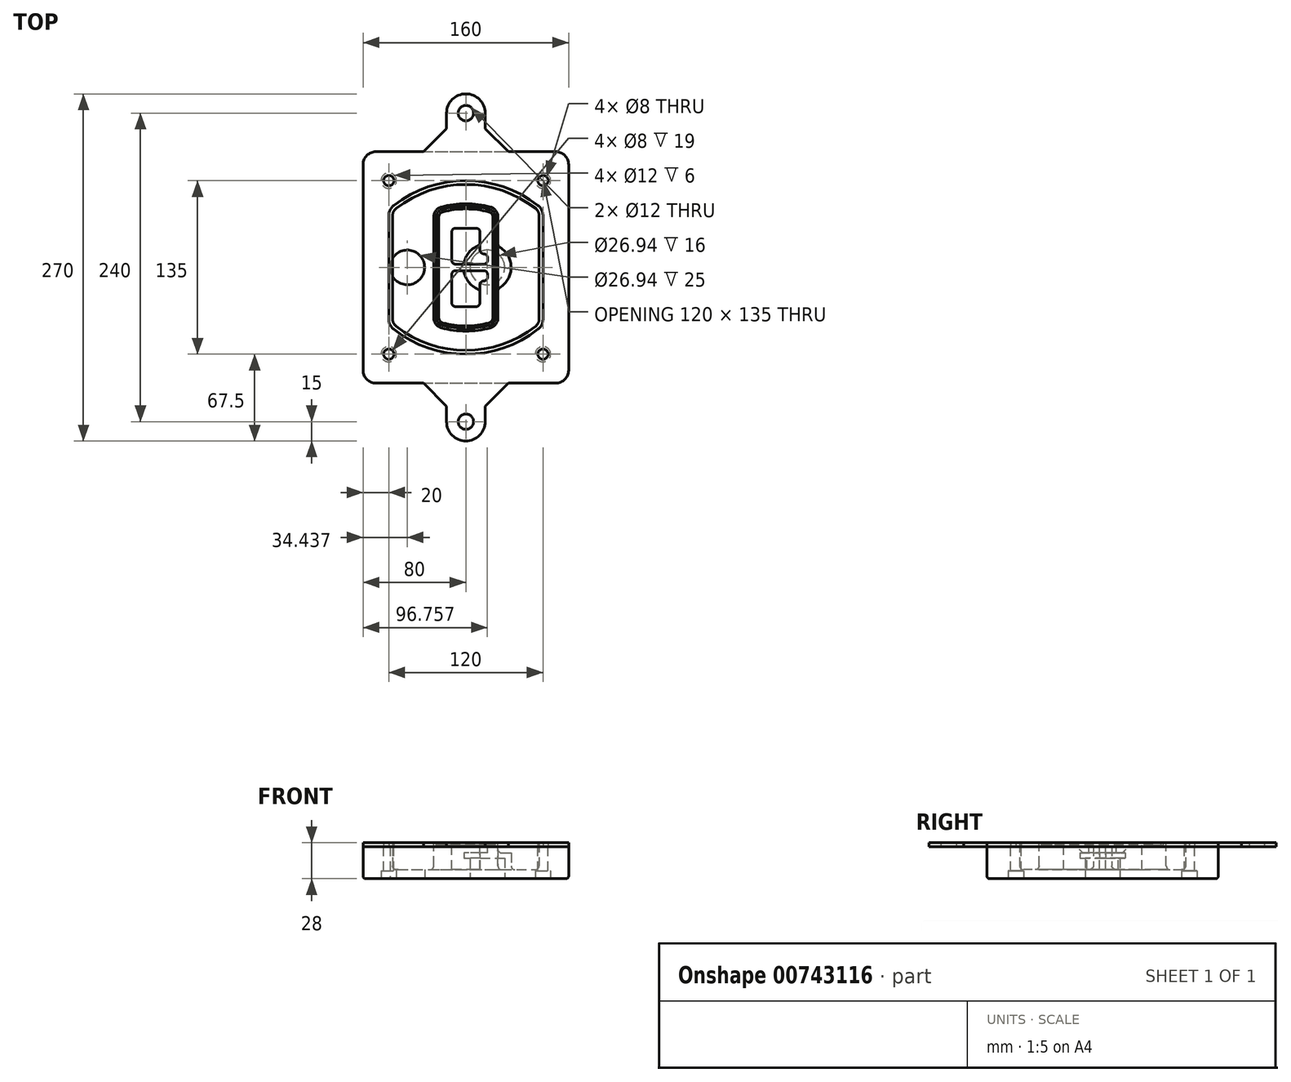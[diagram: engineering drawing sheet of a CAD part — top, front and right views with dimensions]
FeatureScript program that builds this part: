
annotation { "Feature Type Name" : "Feature", "Feature Type Description" : "" }
export const myFeature = defineFeature(function(context is Context, id is Id, definition is map)
    precondition{}
    {
        {
            var Q0;
            Q0=qCreatedBy(makeId("Top.planeOp"),FACE);
            var sketch = newSketch(context, id + "F0", { "sketchPlane" : qUnion([Q0])});
            skPoint(sketch, "E0.rect.middle", {"position": v(0, 0) * mm});
            skLineSegment(sketch, "E1.bottom", {"start": v(-70, -90) * mm, "end": v(70, -90) * mm});
            skLineSegment(sketch, "E1.top", {"start": v(-70, 90) * mm, "end": v(70, 90) * mm});
            skLineSegment(sketch, "E1.left", {"start": v(-80, -80) * mm, "end": v(-80, 80) * mm});
            skLineSegment(sketch, "E1.right", {"start": v(80, -80) * mm, "end": v(80, 80) * mm});
            skLineSegment(sketch, "E2", {"start": v(-80, 90) * mm, "end": v(80, -90) * mm, "construction": true});
            skLineSegment(sketch, "E3", {"start": v(80, 90) * mm, "end": v(-80, -90) * mm, "construction": true});
            skCircle(sketch, "E4", {"center": v(-60, 67.5) * mm, "radius": 4 * mm});
            skCircle(sketch, "E5", {"center": v(60, 67.5) * mm, "radius": 4 * mm});
            skCircle(sketch, "E6", {"center": v(60, -67.5) * mm, "radius": 4 * mm});
            skCircle(sketch, "E7", {"center": v(-60, -67.5) * mm, "radius": 4 * mm});
            skLineSegment(sketch, "E8", {"start": v(-60, 67.5) * mm, "end": v(60, 67.5) * mm, "construction": true});
            skLineSegment(sketch, "E9", {"start": v(60, 67.5) * mm, "end": v(60, -67.5) * mm, "construction": true});
            skLineSegment(sketch, "E10", {"start": v(60, -67.5) * mm, "end": v(-60, -67.5) * mm, "construction": true});
            skLineSegment(sketch, "E11", {"start": v(-60, -67.5) * mm, "end": v(-60, 67.5) * mm, "construction": true});
            skLineSegment(sketch, "E12", {"start": v(-60, 40.3) * mm, "end": v(-60, -40.3) * mm});
            skLineSegment(sketch, "E13", {"start": v(60, 40.3) * mm, "end": v(60, -40.3) * mm});
            skArc(sketch, "E14", {"start": v(56.15, 48.18) * mm, "mid": v(0, 67.5) * mm, "end": v(-56.15, 48.18) * mm});
            skArc(sketch, "E15", {"start": v(-56.15, -48.18) * mm, "mid": v(0, -67.5) * mm, "end": v(56.15, -48.18) * mm});
            skLineSegment(sketch, "E16", {"start": v(-60, 0) * mm, "end": v(60, 0) * mm, "construction": true});
            skPoint(sketch, "E17.visualSharp", {"position": v(-60, -45) * mm});
            skArc(sketch, "E17.filletArc", {"start": v(-60, -40.3) * mm, "mid": v(-58.99, -44.68) * mm, "end": v(-56.15, -48.18) * mm});
            skPoint(sketch, "E18.visualSharp", {"position": v(-60, 45) * mm});
            skArc(sketch, "E18.filletArc", {"start": v(-56.15, 48.18) * mm, "mid": v(-58.99, 44.68) * mm, "end": v(-60, 40.3) * mm});
            skPoint(sketch, "E19.visualSharp", {"position": v(60, 45) * mm});
            skArc(sketch, "E19.filletArc", {"start": v(60, 40.3) * mm, "mid": v(58.99, 44.68) * mm, "end": v(56.15, 48.18) * mm});
            skPoint(sketch, "E20.visualSharp", {"position": v(60, -45) * mm});
            skArc(sketch, "E20.filletArc", {"start": v(56.15, -48.18) * mm, "mid": v(58.99, -44.68) * mm, "end": v(60, -40.3) * mm});
            skPoint(sketch, "E21.visualSharp", {"position": v(-80, 90) * mm});
            skArc(sketch, "E21.filletArc", {"start": v(-70, 90) * mm, "mid": v(-77.07, 87.07) * mm, "end": v(-80, 80) * mm});
            skPoint(sketch, "E22.visualSharp", {"position": v(80, 90) * mm});
            skArc(sketch, "E22.filletArc", {"start": v(80, 80) * mm, "mid": v(77.07, 87.07) * mm, "end": v(70, 90) * mm});
            skPoint(sketch, "E23.visualSharp", {"position": v(80, -90) * mm});
            skArc(sketch, "E23.filletArc", {"start": v(70, -90) * mm, "mid": v(77.07, -87.07) * mm, "end": v(80, -80) * mm});
            skPoint(sketch, "E24.visualSharp", {"position": v(-80, -90) * mm});
            skArc(sketch, "E24.filletArc", {"start": v(-80, -80) * mm, "mid": v(-77.07, -87.07) * mm, "end": v(-70, -90) * mm});
            skArc(sketch, "E25.0", {"start": v(57, 40.3) * mm, "mid": v(56.3, 43.36) * mm, "end": v(54.3, 45.81) * mm});
            skLineSegment(sketch, "E25.1", {"start": v(57, 40.3) * mm, "end": v(57, -40.3) * mm});
            skArc(sketch, "E25.2", {"start": v(54.3, -45.81) * mm, "mid": v(56.3, -43.36) * mm, "end": v(57, -40.3) * mm});
            skArc(sketch, "E25.3", {"start": v(-54.3, -45.81) * mm, "mid": v(0, -64.5) * mm, "end": v(54.3, -45.81) * mm});
            skArc(sketch, "E25.4", {"start": v(-57, -40.3) * mm, "mid": v(-56.3, -43.36) * mm, "end": v(-54.3, -45.81) * mm});
            skArc(sketch, "E25.5", {"start": v(54.3, 45.81) * mm, "mid": v(0, 64.5) * mm, "end": v(-54.3, 45.81) * mm});
            skLineSegment(sketch, "E25.6", {"start": v(-57, 40.3) * mm, "end": v(-57, -40.3) * mm});
            skArc(sketch, "E25.7", {"start": v(-54.3, 45.81) * mm, "mid": v(-56.3, 43.36) * mm, "end": v(-57, 40.3) * mm});
            skArc(sketch, "E26.0", {"start": v(-58.62, 51.33) * mm, "mid": v(-62.58, 46.43) * mm, "end": v(-64, 40.3) * mm});
            skArc(sketch, "E26.1", {"start": v(58.62, 51.33) * mm, "mid": v(0, 71.5) * mm, "end": v(-58.62, 51.33) * mm});
            skArc(sketch, "E26.2", {"start": v(64, 40.3) * mm, "mid": v(62.58, 46.43) * mm, "end": v(58.62, 51.33) * mm});
            skLineSegment(sketch, "E26.3", {"start": v(64, 40.3) * mm, "end": v(64, -40.3) * mm});
            skArc(sketch, "E26.4", {"start": v(58.62, -51.33) * mm, "mid": v(62.58, -46.43) * mm, "end": v(64, -40.3) * mm});
            skLineSegment(sketch, "E26.5", {"start": v(-64, 40.3) * mm, "end": v(-64, -40.3) * mm});
            skArc(sketch, "E26.6", {"start": v(-58.62, -51.33) * mm, "mid": v(0, -71.5) * mm, "end": v(58.62, -51.33) * mm});
            skArc(sketch, "E26.7", {"start": v(-64, -40.3) * mm, "mid": v(-62.58, -46.43) * mm, "end": v(-58.62, -51.33) * mm});
            skSolve(sketch);
        }
        {
            var Q0;
            Q0=makeQuery(id+"F0.imprint","IMPRINT",FACE,{"disambiguationData":[TD([[makeQuery(id+"F0.imprint","IMPRINT",EDGE,{"derivedFrom":sQuery(id+"F0.wireOp",EDGE,"E1.bottom")}),1.0]])]});
            var Q1;
            Q1=makeQuery(id+"F0.imprint","IMPRINT",FACE,{"disambiguationData":[TD([[makeQuery(id+"F0.imprint","IMPRINT",EDGE,{"derivedFrom":sQuery(id+"F0.wireOp",EDGE,"E12")}),1.0]])]});
            var Q2;
            Q2=makeQuery(id+"F0.imprint","IMPRINT",FACE,{"disambiguationData":[TD([[makeQuery(id+"F0.imprint","IMPRINT",EDGE,{"derivedFrom":sQuery(id+"F0.wireOp",EDGE,"E25.0")}),1.0]])]});
            var Q3;
            Q3=makeQuery(id+"F0.imprint","IMPRINT",FACE,{"disambiguationData":[TD([[makeQuery(id+"F0.imprint","IMPRINT",EDGE,{"derivedFrom":sQuery(id+"F0.wireOp",EDGE,"E12")}),-1.0]])]});
            extrude(context, id + "F1", {"entities" : qUnion([Q0, Q1, Q2, Q3]), "oppositeDirection" : true, "depth" : 25 * mm});
        }
        {
            var Q0;
            Q0=makeQuery(id+"F0.imprint","IMPRINT",FACE,{"disambiguationData":[TD([[makeQuery(id+"F0.imprint","IMPRINT",EDGE,{"derivedFrom":sQuery(id+"F0.wireOp",EDGE,"E12")}),1.0]])]});
            extrude(context, id + "F2", {"entities" : qUnion([Q0]), "operationType" : NewBodyOperationType.ADD, "depth" : 3 * mm});
        }
        {
            var Q0;
            Q0=makeQuery(id+"F0.imprint","IMPRINT",FACE,{"disambiguationData":[TD([[makeQuery(id+"F0.imprint","IMPRINT",EDGE,{"derivedFrom":sQuery(id+"F0.wireOp",EDGE,"E25.0")}),1.0]])]});
            extrude(context, id + "F3", {"entities" : qUnion([Q0]), "operationType" : NewBodyOperationType.REMOVE, "oppositeDirection" : true, "depth" : 18 * mm});
        }
        {
            var Q0;
            Q0=makeQuery(id+"F2.opExtrude","CAP_FACE",FACE,{"disambiguationData":[OSD([sQuery(id+"F0.wireOp",EDGE,"E12"),sQuery(id+"F0.wireOp",EDGE,"E13"),sQuery(id+"F0.wireOp",EDGE,"E14"),sQuery(id+"F0.wireOp",EDGE,"E15"),sQuery(id+"F0.wireOp",EDGE,"E17.filletArc"),sQuery(id+"F0.wireOp",EDGE,"E18.filletArc"),sQuery(id+"F0.wireOp",EDGE,"E19.filletArc"),sQuery(id+"F0.wireOp",EDGE,"E20.filletArc"),sQuery(id+"F0.wireOp",EDGE,"E25.0"),sQuery(id+"F0.wireOp",EDGE,"E25.1"),sQuery(id+"F0.wireOp",EDGE,"E25.2"),sQuery(id+"F0.wireOp",EDGE,"E25.3"),sQuery(id+"F0.wireOp",EDGE,"E25.4"),sQuery(id+"F0.wireOp",EDGE,"E25.5"),sQuery(id+"F0.wireOp",EDGE,"E25.6"),sQuery(id+"F0.wireOp",EDGE,"E25.7")])],"isStart":false});
            var sketch = newSketch(context, id + "F4", { "sketchPlane" : qUnion([Q0])});
            skArc(sketch, "E27.0", {"start": v(-19.08, -46.97) * mm, "mid": v(0, -49.5) * mm, "end": v(19.08, -46.97) * mm});
            skArc(sketch, "E28.0", {"start": v(19.08, 46.97) * mm, "mid": v(0, 49.5) * mm, "end": v(-19.08, 46.97) * mm});
            skLineSegment(sketch, "E29", {"start": v(-25, 39.25) * mm, "end": v(-25, -39.25) * mm});
            skLineSegment(sketch, "E30", {"start": v(25, 39.25) * mm, "end": v(25, -39.25) * mm});
            skLineSegment(sketch, "E31", {"start": v(-25, 45.1) * mm, "end": v(25, 45.1) * mm, "construction": true});
            skLineSegment(sketch, "E32", {"start": v(-25, -45.1) * mm, "end": v(25, -45.1) * mm, "construction": true});
            skPoint(sketch, "E33.visualSharp", {"position": v(-25, 45.1) * mm});
            skArc(sketch, "E33.filletArc", {"start": v(-19.08, 46.97) * mm, "mid": v(-23.35, 44.11) * mm, "end": v(-25, 39.25) * mm});
            skPoint(sketch, "E34.visualSharp", {"position": v(25, 45.1) * mm});
            skArc(sketch, "E34.filletArc", {"start": v(25, 39.25) * mm, "mid": v(23.35, 44.11) * mm, "end": v(19.08, 46.97) * mm});
            skPoint(sketch, "E35.visualSharp", {"position": v(25, -45.1) * mm});
            skArc(sketch, "E35.filletArc", {"start": v(19.08, -46.97) * mm, "mid": v(23.35, -44.11) * mm, "end": v(25, -39.25) * mm});
            skPoint(sketch, "E36.visualSharp", {"position": v(-25, -45.1) * mm});
            skArc(sketch, "E36.filletArc", {"start": v(-25, -39.25) * mm, "mid": v(-23.35, -44.11) * mm, "end": v(-19.08, -46.97) * mm});
            skArc(sketch, "E37.0", {"start": v(54.3, 45.81) * mm, "mid": v(0, 64.5) * mm, "end": v(-54.3, 45.81) * mm});
            skArc(sketch, "E37.1", {"start": v(-54.3, 45.81) * mm, "mid": v(-56.3, 43.36) * mm, "end": v(-57, 40.3) * mm});
            skLineSegment(sketch, "E37.2", {"start": v(-57, 40.3) * mm, "end": v(-57, -40.3) * mm});
            skArc(sketch, "E37.3", {"start": v(-57, -40.3) * mm, "mid": v(-56.3, -43.36) * mm, "end": v(-54.3, -45.81) * mm});
            skArc(sketch, "E37.4", {"start": v(-54.3, -45.81) * mm, "mid": v(0, -64.5) * mm, "end": v(54.3, -45.81) * mm});
            skArc(sketch, "E37.5", {"start": v(54.3, -45.81) * mm, "mid": v(56.3, -43.36) * mm, "end": v(57, -40.3) * mm});
            skLineSegment(sketch, "E37.6", {"start": v(57, 40.3) * mm, "end": v(57, -40.3) * mm});
            skArc(sketch, "E37.7", {"start": v(57, 40.3) * mm, "mid": v(56.3, 43.36) * mm, "end": v(54.3, 45.81) * mm});
            skLineSegment(sketch, "E38.0", {"start": v(23, 39.25) * mm, "end": v(23, -39.25) * mm});
            skArc(sketch, "E38.1", {"start": v(18.56, -45.04) * mm, "mid": v(21.76, -42.9) * mm, "end": v(23, -39.25) * mm});
            skArc(sketch, "E38.2", {"start": v(-18.56, -45.04) * mm, "mid": v(0, -47.5) * mm, "end": v(18.56, -45.04) * mm});
            skArc(sketch, "E38.3", {"start": v(-23, -39.25) * mm, "mid": v(-21.76, -42.9) * mm, "end": v(-18.56, -45.04) * mm});
            skLineSegment(sketch, "E38.4", {"start": v(-23, 39.25) * mm, "end": v(-23, -39.25) * mm});
            skArc(sketch, "E38.5", {"start": v(23, 39.25) * mm, "mid": v(21.76, 42.9) * mm, "end": v(18.56, 45.04) * mm});
            skArc(sketch, "E38.6", {"start": v(-18.56, 45.04) * mm, "mid": v(-21.76, 42.9) * mm, "end": v(-23, 39.25) * mm});
            skArc(sketch, "E38.7", {"start": v(18.56, 45.04) * mm, "mid": v(0, 47.5) * mm, "end": v(-18.56, 45.04) * mm});
            skArc(sketch, "E39.0", {"start": v(21, 39.25) * mm, "mid": v(20.18, 41.68) * mm, "end": v(18.04, 43.1) * mm});
            skLineSegment(sketch, "E39.1", {"start": v(21, 39.25) * mm, "end": v(21, -39.25) * mm});
            skArc(sketch, "E39.2", {"start": v(18.04, -43.1) * mm, "mid": v(20.18, -41.68) * mm, "end": v(21, -39.25) * mm});
            skArc(sketch, "E39.3", {"start": v(-18.04, -43.1) * mm, "mid": v(0, -45.5) * mm, "end": v(18.04, -43.1) * mm});
            skArc(sketch, "E39.4", {"start": v(-21, -39.25) * mm, "mid": v(-20.18, -41.68) * mm, "end": v(-18.04, -43.1) * mm});
            skArc(sketch, "E39.5", {"start": v(18.04, 43.1) * mm, "mid": v(0, 45.5) * mm, "end": v(-18.04, 43.1) * mm});
            skLineSegment(sketch, "E39.6", {"start": v(-21, 39.25) * mm, "end": v(-21, -39.25) * mm});
            skArc(sketch, "E39.7", {"start": v(-18.04, 43.1) * mm, "mid": v(-20.18, 41.68) * mm, "end": v(-21, 39.25) * mm});
            skLineSegment(sketch, "E40", {"start": v(-25, 0) * mm, "end": v(25, 0) * mm, "construction": true});
            skLineSegment(sketch, "E41", {"start": v(-11, 5.5) * mm, "end": v(-11, 27.5) * mm});
            skLineSegment(sketch, "E42", {"start": v(-8, 30.5) * mm, "end": v(8, 30.5) * mm});
            skLineSegment(sketch, "E43", {"start": v(11, 27.5) * mm, "end": v(11, 13.5) * mm});
            skLineSegment(sketch, "E44", {"start": v(14, 10.5) * mm, "end": v(14, 10.5) * mm});
            skLineSegment(sketch, "E45", {"start": v(17, 7.5) * mm, "end": v(17, 5.5) * mm});
            skLineSegment(sketch, "E46", {"start": v(14, 2.5) * mm, "end": v(-8, 2.5) * mm});
            skPoint(sketch, "E47.visualSharp", {"position": v(-11, 30.5) * mm});
            skArc(sketch, "E47.filletArc", {"start": v(-8, 30.5) * mm, "mid": v(-10.12, 29.62) * mm, "end": v(-11, 27.5) * mm});
            skPoint(sketch, "E48.visualSharp", {"position": v(11, 30.5) * mm});
            skArc(sketch, "E48.filletArc", {"start": v(11, 27.5) * mm, "mid": v(10.12, 29.62) * mm, "end": v(8, 30.5) * mm});
            skPoint(sketch, "E49.visualSharp", {"position": v(11, 10.5) * mm});
            skArc(sketch, "E49.filletArc", {"start": v(11, 13.5) * mm, "mid": v(11.88, 11.38) * mm, "end": v(14, 10.5) * mm});
            skPoint(sketch, "E50.visualSharp", {"position": v(17, 10.5) * mm});
            skArc(sketch, "E50.filletArc", {"start": v(17, 7.5) * mm, "mid": v(16.12, 9.62) * mm, "end": v(14, 10.5) * mm});
            skPoint(sketch, "E51.visualSharp", {"position": v(17, 2.5) * mm});
            skArc(sketch, "E51.filletArc", {"start": v(14, 2.5) * mm, "mid": v(16.12, 3.38) * mm, "end": v(17, 5.5) * mm});
            skPoint(sketch, "E52.visualSharp", {"position": v(-11, 2.5) * mm});
            skArc(sketch, "E52.filletArc", {"start": v(-11, 5.5) * mm, "mid": v(-10.12, 3.38) * mm, "end": v(-8, 2.5) * mm});
            skLineSegment(sketch, "E53.0.MirrorCS", {"start": v(14, -2.5) * mm, "end": v(-8, -2.5) * mm});
            skArc(sketch, "E54.0.MirrorCS", {"start": v(-11, -5.5) * mm, "mid": v(-10.12, -3.38) * mm, "end": v(-8, -2.5) * mm});
            skLineSegment(sketch, "E55.0.MirrorCS", {"start": v(-11, -5.5) * mm, "end": v(-11, -27.5) * mm});
            skArc(sketch, "E56.0.MirrorCS", {"start": v(-8, -30.5) * mm, "mid": v(-10.12, -29.62) * mm, "end": v(-11, -27.5) * mm});
            skLineSegment(sketch, "E57.0.MirrorCS", {"start": v(-8, -30.5) * mm, "end": v(8, -30.5) * mm});
            skArc(sketch, "E58.0.MirrorCS", {"start": v(11, -27.5) * mm, "mid": v(10.12, -29.62) * mm, "end": v(8, -30.5) * mm});
            skLineSegment(sketch, "E59.0.MirrorCS", {"start": v(11, -27.5) * mm, "end": v(11, -13.5) * mm});
            skArc(sketch, "E60.0.MirrorCS", {"start": v(11, -13.5) * mm, "mid": v(11.88, -11.38) * mm, "end": v(14, -10.5) * mm});
            skArc(sketch, "E61.0.MirrorCS", {"start": v(17, -7.5) * mm, "mid": v(16.12, -9.62) * mm, "end": v(14, -10.5) * mm});
            skLineSegment(sketch, "E62.0.MirrorCS", {"start": v(17, -7.5) * mm, "end": v(17, -5.5) * mm});
            skArc(sketch, "E63.0.MirrorCS", {"start": v(14, -2.5) * mm, "mid": v(16.12, -3.38) * mm, "end": v(17, -5.5) * mm});
            skSolve(sketch);
        }
        {
            var Q0;
            Q0=makeQuery(id+"F4.imprint","IMPRINT",FACE,{"disambiguationData":[TD([[makeQuery(id+"F4.imprint","IMPRINT",EDGE,{"derivedFrom":sQuery(id+"F4.wireOp",EDGE,"E27.0")}),1.0]])]});
            var Q1;
            Q1=makeQuery(id+"F4.imprint","IMPRINT",FACE,{"disambiguationData":[TD([[makeQuery(id+"F4.imprint","IMPRINT",EDGE,{"derivedFrom":sQuery(id+"F4.wireOp",EDGE,"E38.0")}),-1.0]])]});
            var Q2;
            Q2=makeQuery(id+"F4.imprint","IMPRINT",FACE,{"disambiguationData":[TD([[makeQuery(id+"F4.imprint","IMPRINT",EDGE,{"derivedFrom":sQuery(id+"F4.wireOp",EDGE,"E39.0")}),1.0]])]});
            extrude(context, id + "F5", {"entities" : qUnion([Q0, Q1, Q2]), "operationType" : NewBodyOperationType.ADD, "endBound" : BoundingType.UP_TO_NEXT, "oppositeDirection" : true, "depth" : 25 * mm});
        }
        {
            var Q0;
            Q0=makeQuery(id+"F4.imprint","IMPRINT",FACE,{"disambiguationData":[TD([[makeQuery(id+"F4.imprint","IMPRINT",EDGE,{"derivedFrom":sQuery(id+"F4.wireOp",EDGE,"E38.0")}),-1.0]])]});
            extrude(context, id + "F6", {"entities" : qUnion([Q0]), "operationType" : NewBodyOperationType.REMOVE, "oppositeDirection" : true, "depth" : 2 * mm});
        }
        {
            var Q0;
            Q0=makeQuery(id+"F1.opExtrude","CAP_FACE",FACE,{"disambiguationData":[OSD([sQuery(id+"F0.wireOp",EDGE,"E1.bottom"),sQuery(id+"F0.wireOp",EDGE,"E1.top"),sQuery(id+"F0.wireOp",EDGE,"E1.left"),sQuery(id+"F0.wireOp",EDGE,"E1.right"),sQuery(id+"F0.wireOp",EDGE,"E4"),sQuery(id+"F0.wireOp",EDGE,"E5"),sQuery(id+"F0.wireOp",EDGE,"E6"),sQuery(id+"F0.wireOp",EDGE,"E7"),sQuery(id+"F0.wireOp",EDGE,"E21.filletArc"),sQuery(id+"F0.wireOp",EDGE,"E22.filletArc"),sQuery(id+"F0.wireOp",EDGE,"E23.filletArc"),sQuery(id+"F0.wireOp",EDGE,"E24.filletArc")])],"isStart":false});
            var sketch = newSketch(context, id + "F7", { "sketchPlane" : qUnion([Q0])});
            skCircle(sketch, "E64", {"center": v(16.76, 0) * mm, "radius": 13.47 * mm});
            skCircle(sketch, "E65", {"center": v(-45.56, 0) * mm, "radius": 13.47 * mm});
            skLineSegment(sketch, "E66", {"start": v(80, 0) * mm, "end": v(-80, 0) * mm});
            skCircle(sketch, "E67", {"center": v(16.76, 0) * mm, "radius": 18.47 * mm});
            skCircle(sketch, "E68", {"center": v(60, -67.5) * mm, "radius": 6 * mm});
            skCircle(sketch, "E69", {"center": v(-60, -67.5) * mm, "radius": 6 * mm});
            skCircle(sketch, "E70", {"center": v(-60, 67.5) * mm, "radius": 6 * mm});
            skCircle(sketch, "E71", {"center": v(60, 67.5) * mm, "radius": 6 * mm});
            skSolve(sketch);
        }
        {
            var Q0;
            {var subQ1=sQuery(id+"F7.wireOp",EDGE,"E66");var subQ4=sQuery(id+"F7.wireOp",EDGE,"E64");var subQ6=makeQuery(id+"F7.imprint","INTERSECT",VERTEX,{"disambiguationData":[OD(0.0)],"derivedFrom":[subQ4,subQ1]});Q0=makeQuery(id+"F7.imprint","IMPRINT",FACE,{"disambiguationData":[TD([[makeQuery(id+"F7.imprint","IMPRINT",EDGE,{"disambiguationData":[TD([[subQ6,-1.0]])],"derivedFrom":subQ4}),-1.0]])]});}
            var Q1;
            {var subQ0=sQuery(id+"F7.wireOp",EDGE,"E66");var subQ1=sQuery(id+"F7.wireOp",EDGE,"E64");var subQ3=makeQuery(id+"F7.imprint","INTERSECT",VERTEX,{"disambiguationData":[OD(0.0)],"derivedFrom":[subQ1,subQ0]});Q1=makeQuery(id+"F7.imprint","IMPRINT",FACE,{"disambiguationData":[TD([[makeQuery(id+"F7.imprint","IMPRINT",EDGE,{"disambiguationData":[TD([[subQ3,-1.0]])],"derivedFrom":subQ1}),1.0]])]});}
            var Q2;
            {var subQ0=sQuery(id+"F7.wireOp",EDGE,"E66");var subQ1=sQuery(id+"F7.wireOp",EDGE,"E64");var subQ3=makeQuery(id+"F7.imprint","INTERSECT",VERTEX,{"disambiguationData":[OD(0.0)],"derivedFrom":[subQ1,subQ0]});Q2=makeQuery(id+"F7.imprint","IMPRINT",FACE,{"disambiguationData":[TD([[makeQuery(id+"F7.imprint","IMPRINT",EDGE,{"disambiguationData":[TD([[subQ3,1.0]])],"derivedFrom":subQ1}),1.0]])]});}
            var Q3;
            {var subQ1=sQuery(id+"F7.wireOp",EDGE,"E66");var subQ4=sQuery(id+"F7.wireOp",EDGE,"E64");var subQ6=makeQuery(id+"F7.imprint","INTERSECT",VERTEX,{"disambiguationData":[OD(0.0)],"derivedFrom":[subQ4,subQ1]});Q3=makeQuery(id+"F7.imprint","IMPRINT",FACE,{"disambiguationData":[TD([[makeQuery(id+"F7.imprint","IMPRINT",EDGE,{"disambiguationData":[TD([[subQ6,1.0]])],"derivedFrom":subQ4}),-1.0]])]});}
            extrude(context, id + "F8", {"entities" : qUnion([Q0, Q1, Q2, Q3]), "operationType" : NewBodyOperationType.ADD, "oppositeDirection" : true, "depth" : 20 * mm, "offsetDistance" : 25 * mm});
        }
        {
            var Q0;
            {var subQ0=sQuery(id+"F7.wireOp",EDGE,"E66");var subQ1=sQuery(id+"F7.wireOp",EDGE,"E64");var subQ3=makeQuery(id+"F7.imprint","INTERSECT",VERTEX,{"disambiguationData":[OD(0.0)],"derivedFrom":[subQ1,subQ0]});Q0=makeQuery(id+"F7.imprint","IMPRINT",FACE,{"disambiguationData":[TD([[makeQuery(id+"F7.imprint","IMPRINT",EDGE,{"disambiguationData":[TD([[subQ3,-1.0]])],"derivedFrom":subQ1}),1.0]])]});}
            var Q1;
            {var subQ0=sQuery(id+"F7.wireOp",EDGE,"E66");var subQ1=sQuery(id+"F7.wireOp",EDGE,"E64");var subQ3=makeQuery(id+"F7.imprint","INTERSECT",VERTEX,{"disambiguationData":[OD(0.0)],"derivedFrom":[subQ1,subQ0]});Q1=makeQuery(id+"F7.imprint","IMPRINT",FACE,{"disambiguationData":[TD([[makeQuery(id+"F7.imprint","IMPRINT",EDGE,{"disambiguationData":[TD([[subQ3,1.0]])],"derivedFrom":subQ1}),1.0]])]});}
            extrude(context, id + "F9", {"entities" : qUnion([Q0, Q1]), "operationType" : NewBodyOperationType.REMOVE, "oppositeDirection" : true, "depth" : 16 * mm, "offsetDistance" : 25 * mm});
        }
        {
            var Q0;
            {var subQ0=sQuery(id+"F7.wireOp",EDGE,"E66");var subQ1=sQuery(id+"F7.wireOp",EDGE,"E65");var subQ3=makeQuery(id+"F7.imprint","INTERSECT",VERTEX,{"disambiguationData":[OD(0.0)],"derivedFrom":[subQ1,subQ0]});Q0=makeQuery(id+"F7.imprint","IMPRINT",FACE,{"disambiguationData":[TD([[makeQuery(id+"F7.imprint","IMPRINT",EDGE,{"disambiguationData":[TD([[subQ3,-1.0]])],"derivedFrom":subQ1}),1.0]])]});}
            var Q1;
            {var subQ0=sQuery(id+"F7.wireOp",EDGE,"E66");var subQ1=sQuery(id+"F7.wireOp",EDGE,"E65");var subQ3=makeQuery(id+"F7.imprint","INTERSECT",VERTEX,{"disambiguationData":[OD(0.0)],"derivedFrom":[subQ1,subQ0]});Q1=makeQuery(id+"F7.imprint","IMPRINT",FACE,{"disambiguationData":[TD([[makeQuery(id+"F7.imprint","IMPRINT",EDGE,{"disambiguationData":[TD([[subQ3,1.0]])],"derivedFrom":subQ1}),1.0]])]});}
            extrude(context, id + "F10", {"entities" : qUnion([Q0, Q1]), "operationType" : NewBodyOperationType.REMOVE, "oppositeDirection" : true, "depth" : 25 * mm, "offsetDistance" : 25 * mm});
        }
        {
            var Q0;
            Q0=makeQuery(id+"F7.imprint","IMPRINT",FACE,{"disambiguationData":[TD([[makeQuery(id+"F7.imprint","IMPRINT",EDGE,{"derivedFrom":sQuery(id+"F7.wireOp",EDGE,"E68")}),1.0]])]});
            var Q1;
            Q1=makeQuery(id+"F7.imprint","IMPRINT",FACE,{"disambiguationData":[TD([[makeQuery(id+"F7.imprint","IMPRINT",EDGE,{"derivedFrom":makeQuery(id+"F1.opExtrude","CAP_EDGE",EDGE,{"disambiguationData":[OSD([sQuery(id+"F0.wireOp",EDGE,"E5")])],"isStart":false})}),-1.0]])]});
            var Q2;
            Q2=makeQuery(id+"F7.imprint","IMPRINT",FACE,{"disambiguationData":[TD([[makeQuery(id+"F7.imprint","IMPRINT",EDGE,{"derivedFrom":sQuery(id+"F7.wireOp",EDGE,"E69")}),1.0]])]});
            var Q3;
            Q3=makeQuery(id+"F7.imprint","IMPRINT",FACE,{"disambiguationData":[TD([[makeQuery(id+"F7.imprint","IMPRINT",EDGE,{"derivedFrom":makeQuery(id+"F1.opExtrude","CAP_EDGE",EDGE,{"disambiguationData":[OSD([sQuery(id+"F0.wireOp",EDGE,"E4")])],"isStart":false})}),-1.0]])]});
            var Q4;
            Q4=makeQuery(id+"F7.imprint","IMPRINT",FACE,{"disambiguationData":[TD([[makeQuery(id+"F7.imprint","IMPRINT",EDGE,{"derivedFrom":sQuery(id+"F7.wireOp",EDGE,"E70")}),1.0]])]});
            var Q5;
            Q5=makeQuery(id+"F7.imprint","IMPRINT",FACE,{"disambiguationData":[TD([[makeQuery(id+"F7.imprint","IMPRINT",EDGE,{"derivedFrom":makeQuery(id+"F1.opExtrude","CAP_EDGE",EDGE,{"disambiguationData":[OSD([sQuery(id+"F0.wireOp",EDGE,"E7")])],"isStart":false})}),-1.0]])]});
            var Q6;
            Q6=makeQuery(id+"F7.imprint","IMPRINT",FACE,{"disambiguationData":[TD([[makeQuery(id+"F7.imprint","IMPRINT",EDGE,{"derivedFrom":sQuery(id+"F7.wireOp",EDGE,"E71")}),1.0]])]});
            var Q7;
            Q7=makeQuery(id+"F7.imprint","IMPRINT",FACE,{"disambiguationData":[TD([[makeQuery(id+"F7.imprint","IMPRINT",EDGE,{"derivedFrom":makeQuery(id+"F1.opExtrude","CAP_EDGE",EDGE,{"disambiguationData":[OSD([sQuery(id+"F0.wireOp",EDGE,"E6")])],"isStart":false})}),-1.0]])]});
            extrude(context, id + "F11", {"entities" : qUnion([Q0, Q1, Q2, Q3, Q4, Q5, Q6, Q7]), "operationType" : NewBodyOperationType.REMOVE, "oppositeDirection" : true, "depth" : 6 * mm});
        }
        {
            var Q0;
            Q0=makeQuery(id+"F9.boolean.opBoolean","COPY",FACE,{"derivedFrom":makeQuery(id+"F9.opExtrude","CAP_FACE",FACE,{"disambiguationData":[OSD([sQuery(id+"F7.wireOp",EDGE,"E64")])],"isStart":false})});
            var sketch = newSketch(context, id + "F12", { "sketchPlane" : qUnion([Q0])});
            skArc(sketch, "E72.0", {"start": v(11, 17.55) * mm, "mid": v(2.57, 11.82) * mm, "end": v(-1.54, 2.5) * mm});
            skArc(sketch, "E72.1", {"start": v(-1.54, -2.5) * mm, "mid": v(2.57, -11.82) * mm, "end": v(11, -17.55) * mm});
            skLineSegment(sketch, "E73", {"start": v(-1.54, -2.5) * mm, "end": v(14, -2.5) * mm});
            skLineSegment(sketch, "E74.0", {"start": v(14, 2.5) * mm, "end": v(-1.54, 2.5) * mm});
            skArc(sketch, "E74.1", {"start": v(14, 2.5) * mm, "mid": v(16.12, 3.38) * mm, "end": v(17, 5.5) * mm});
            skLineSegment(sketch, "E74.2", {"start": v(17, 7.5) * mm, "end": v(17, 5.5) * mm});
            skArc(sketch, "E74.3", {"start": v(17, 7.5) * mm, "mid": v(16.12, 9.62) * mm, "end": v(14, 10.5) * mm});
            skArc(sketch, "E74.4", {"start": v(11, 13.5) * mm, "mid": v(11.88, 11.38) * mm, "end": v(14, 10.5) * mm});
            skLineSegment(sketch, "E74.5", {"start": v(11, 17.55) * mm, "end": v(11, 13.5) * mm});
            skLineSegment(sketch, "E74.7", {"start": v(14, -2.5) * mm, "end": v(-1.54, -2.5) * mm});
            skArc(sketch, "E74.8", {"start": v(14, -2.5) * mm, "mid": v(16.12, -3.38) * mm, "end": v(17, -5.5) * mm});
            skLineSegment(sketch, "E74.9", {"start": v(17, -7.5) * mm, "end": v(17, -5.5) * mm});
            skArc(sketch, "E74.10", {"start": v(17, -7.5) * mm, "mid": v(16.12, -9.62) * mm, "end": v(14, -10.5) * mm});
            skArc(sketch, "E74.11", {"start": v(11, -13.5) * mm, "mid": v(11.88, -11.38) * mm, "end": v(14, -10.5) * mm});
            skLineSegment(sketch, "E74.12", {"start": v(11, -17.55) * mm, "end": v(11, -13.5) * mm});
            skPoint(sketch, "E75.orphan", {"position": v(11, -27.5) * mm});
            skPoint(sketch, "E76.orphan", {"position": v(-8, -2.5) * mm});
            skPoint(sketch, "E77.orphan", {"position": v(-8, 2.5) * mm});
            skPoint(sketch, "E78.orphan", {"position": v(11, 27.5) * mm});
            skSolve(sketch);
        }
        {
            var Q0;
            {var subQ7=sQuery(id+"F12.wireOp",EDGE,"E72.0");var subQ14=sQuery(id+"F12.wireOp",EDGE,"E72.1");var subQ16=sQuery(id+"F12.wireOp",EDGE,"E74.1");var subQ18=sQuery(id+"F12.wireOp",EDGE,"E74.8");Q0=qUnion([makeQuery(id+"F12.imprint","IMPRINT",FACE,{"disambiguationData":[TD([[makeQuery(id+"F12.imprint","IMPRINT",EDGE,{"derivedFrom":subQ7}),1.0]])]}),makeQuery(id+"F12.imprint","IMPRINT",FACE,{"disambiguationData":[TD([[makeQuery(id+"F12.imprint","IMPRINT",EDGE,{"derivedFrom":subQ14}),1.0]])]}),makeQuery(id+"F12.imprint","IMPRINT",FACE,{"disambiguationData":[TD([[makeQuery(id+"F12.imprint","IMPRINT",EDGE,{"derivedFrom":subQ16}),1.0]])]}),makeQuery(id+"F12.imprint","IMPRINT",FACE,{"disambiguationData":[TD([[makeQuery(id+"F12.imprint","IMPRINT",EDGE,{"derivedFrom":subQ18}),-1.0]])]})]);}
            var Q1;
            Q1=makeQuery(id+"F5.boolean.opBoolean","SPLIT",FACE,{"disambiguationData":[TD([makeQuery(id+"F5.opExtrude","SWEPT_FACE",FACE,{"disambiguationData":[OSD([sQuery(id+"F4.wireOp",EDGE,"E41")])]})])],"derivedFrom":makeQuery(id+"F3.boolean.opBoolean","COPY",FACE,{"derivedFrom":makeQuery(id+"F3.opExtrude","CAP_FACE",FACE,{"disambiguationData":[OSD([sQuery(id+"F0.wireOp",EDGE,"E25.0"),sQuery(id+"F0.wireOp",EDGE,"E25.1"),sQuery(id+"F0.wireOp",EDGE,"E25.2"),sQuery(id+"F0.wireOp",EDGE,"E25.3"),sQuery(id+"F0.wireOp",EDGE,"E25.4"),sQuery(id+"F0.wireOp",EDGE,"E25.5"),sQuery(id+"F0.wireOp",EDGE,"E25.6"),sQuery(id+"F0.wireOp",EDGE,"E25.7")])],"isStart":false})})});
            extrude(context, id + "F13", {"entities" : qUnion([Q0]), "operationType" : NewBodyOperationType.REMOVE, "endBound" : BoundingType.UP_TO_SURFACE, "endBoundEntityFace" : qUnion([Q1]), "depth" : 25 * mm, "offsetDistance" : 25 * mm});
        }
        {
            var Q0;
            Q0=makeQuery(id+"F3.boolean.opBoolean","COPY",EDGE,{"derivedFrom":makeQuery(id+"F3.opExtrude","CAP_EDGE",EDGE,{"disambiguationData":[OSD([sQuery(id+"F0.wireOp",EDGE,"E25.6")])],"isStart":false})});
            var Q1;
            Q1=makeQuery(id+"F8.boolean.opBoolean","INTERSECT",EDGE,{"derivedFrom":[makeQuery(id+"F5.opExtrude","SWEPT_FACE",FACE,{"disambiguationData":[OSD([sQuery(id+"F4.wireOp",EDGE,"E30")])]}),makeQuery(id+"F8.opExtrude","CAP_FACE",FACE,{"disambiguationData":[OSD([sQuery(id+"F7.wireOp",EDGE,"E67")])],"isStart":false})]});
            var Q2;
            Q2=makeQuery(id+"F8.boolean.opBoolean","INTERSECT",EDGE,{"disambiguationData":[OD(1.0)],"derivedFrom":[makeQuery(id+"F5.opExtrude","SWEPT_FACE",FACE,{"disambiguationData":[OSD([sQuery(id+"F4.wireOp",EDGE,"E30")])]}),makeQuery(id+"F8.opExtrude","SWEPT_FACE",FACE,{"disambiguationData":[OSD([sQuery(id+"F7.wireOp",EDGE,"E67")])]})]});
            var Q3;
            {var subQ0=sQuery(id+"F4.wireOp",EDGE,"E30");Q3=makeQuery(id+"F8.boolean.opBoolean","SPLIT",EDGE,{"disambiguationData":[TD([makeQuery(id+"F5.opExtrude","SWEPT_FACE",FACE,{"disambiguationData":[OSD([sQuery(id+"F4.wireOp",EDGE,"E35.filletArc")])]})])],"derivedFrom":makeQuery(id+"F5.opExtrude","CAP_EDGE",EDGE,{"disambiguationData":[OSD([subQ0])],"isStart":false})});}
            var Q4;
            {var subQ0=sQuery(id+"F0.wireOp",EDGE,"E25.7");var subQ1=sQuery(id+"F0.wireOp",EDGE,"E25.1");var subQ2=sQuery(id+"F0.wireOp",EDGE,"E25.6");var subQ3=sQuery(id+"F0.wireOp",EDGE,"E25.5");var subQ4=sQuery(id+"F0.wireOp",EDGE,"E25.4");var subQ5=sQuery(id+"F0.wireOp",EDGE,"E25.0");var subQ6=sQuery(id+"F0.wireOp",EDGE,"E25.2");var subQ7=sQuery(id+"F0.wireOp",EDGE,"E25.3");Q4=makeQuery(id+"F8.boolean.opBoolean","INTERSECT",EDGE,{"derivedFrom":[makeQuery(id+"F5.boolean.opBoolean","SPLIT",FACE,{"disambiguationData":[TD([makeQuery(id+"F2.opExtrude","SWEPT_FACE",FACE,{"disambiguationData":[OSD([subQ5])]})])],"derivedFrom":makeQuery(id+"F3.boolean.opBoolean","COPY",FACE,{"derivedFrom":makeQuery(id+"F3.opExtrude","CAP_FACE",FACE,{"disambiguationData":[OSD([subQ5,subQ1,subQ6,subQ7,subQ4,subQ3,subQ2,subQ0])],"isStart":false})})}),makeQuery(id+"F8.opExtrude","SWEPT_FACE",FACE,{"disambiguationData":[OSD([sQuery(id+"F7.wireOp",EDGE,"E67")])]})]});}
            var Q5;
            Q5=makeQuery(id+"F8.boolean.opBoolean","INTERSECT",EDGE,{"disambiguationData":[OD(0.0)],"derivedFrom":[makeQuery(id+"F5.opExtrude","SWEPT_FACE",FACE,{"disambiguationData":[OSD([sQuery(id+"F4.wireOp",EDGE,"E30")])]}),makeQuery(id+"F8.opExtrude","SWEPT_FACE",FACE,{"disambiguationData":[OSD([sQuery(id+"F7.wireOp",EDGE,"E67")])]})]});
            fillet(context, id + "F14", {"entities" : qUnion([Q0, Q1, Q2, Q3, Q4, Q5]), "radius" : 3 * mm, "tangentPropagation" : true, "allowEdgeOverflow" : false});
        }
        {
            var Q0;
            Q0=makeQuery(id+"F1.opExtrude","CAP_EDGE",EDGE,{"disambiguationData":[OSD([sQuery(id+"F0.wireOp",EDGE,"E1.bottom")])],"isStart":false});
            fillet(context, id + "F15", {"entities" : qUnion([Q0]), "radius" : 2 * mm, "tangentPropagation" : true, "allowEdgeOverflow" : false});
        }
        {
            var Q0;
            {var subQ0=sQuery(id+"F0.wireOp",EDGE,"E21.filletArc");var subQ1=sQuery(id+"F0.wireOp",EDGE,"E7");var subQ2=sQuery(id+"F0.wireOp",EDGE,"E6");var subQ3=sQuery(id+"F0.wireOp",EDGE,"E5");var subQ4=sQuery(id+"F0.wireOp",EDGE,"E4");var subQ5=sQuery(id+"F0.wireOp",EDGE,"E22.filletArc");var subQ6=sQuery(id+"F0.wireOp",EDGE,"E1.bottom");var subQ7=sQuery(id+"F0.wireOp",EDGE,"E1.right");var subQ8=sQuery(id+"F0.wireOp",EDGE,"E1.top");var subQ9=sQuery(id+"F0.wireOp",EDGE,"E1.left");var subQ10=sQuery(id+"F0.wireOp",EDGE,"E23.filletArc");var subQ11=sQuery(id+"F0.wireOp",EDGE,"E24.filletArc");Q0=makeQuery(id+"F2.boolean.opBoolean","SPLIT",FACE,{"disambiguationData":[TD([makeQuery(id+"F1.opExtrude","SWEPT_FACE",FACE,{"disambiguationData":[OSD([subQ6])]})])],"derivedFrom":makeQuery(id+"F1.opExtrude","CAP_FACE",FACE,{"disambiguationData":[OSD([subQ6,subQ8,subQ9,subQ7,subQ4,subQ3,subQ2,subQ1,subQ0,subQ5,subQ10,subQ11])],"isStart":true})});}
            var sketch = newSketch(context, id + "F16", { "sketchPlane" : qUnion([Q0])});
            skLineSegment(sketch, "E79.0", {"start": v(-80, -80) * mm, "end": v(-80, 80) * mm});
            skArc(sketch, "E79.1", {"start": v(-70, 90) * mm, "mid": v(-77.07, 87.07) * mm, "end": v(-80, 80) * mm});
            skLineSegment(sketch, "E79.2", {"start": v(-70, 90) * mm, "end": v(70, 90) * mm});
            skArc(sketch, "E79.3", {"start": v(80, 80) * mm, "mid": v(77.07, 87.07) * mm, "end": v(70, 90) * mm});
            skLineSegment(sketch, "E79.4", {"start": v(80, -80) * mm, "end": v(80, 80) * mm});
            skArc(sketch, "E79.5", {"start": v(70, -90) * mm, "mid": v(77.07, -87.07) * mm, "end": v(80, -80) * mm});
            skLineSegment(sketch, "E79.6", {"start": v(-70, -90) * mm, "end": v(70, -90) * mm});
            skArc(sketch, "E79.7", {"start": v(-80, -80) * mm, "mid": v(-77.07, -87.07) * mm, "end": v(-70, -90) * mm});
            skCircle(sketch, "E79.8", {"center": v(-60, -67.5) * mm, "radius": 4 * mm});
            skCircle(sketch, "E79.9", {"center": v(-60, 67.5) * mm, "radius": 4 * mm});
            skCircle(sketch, "E79.10", {"center": v(60, 67.5) * mm, "radius": 4 * mm});
            skCircle(sketch, "E79.11", {"center": v(60, -67.5) * mm, "radius": 4 * mm});
            skLineSegment(sketch, "E79.12", {"start": v(60, 40.3) * mm, "end": v(60, -40.3) * mm});
            skArc(sketch, "E79.13", {"start": v(-56.15, -48.18) * mm, "mid": v(0, -67.5) * mm, "end": v(56.15, -48.18) * mm});
            skLineSegment(sketch, "E79.14", {"start": v(-60, 40.3) * mm, "end": v(-60, -40.3) * mm});
            skArc(sketch, "E79.15", {"start": v(56.15, 48.18) * mm, "mid": v(0, 67.5) * mm, "end": v(-56.15, 48.18) * mm});
            skArc(sketch, "E79.16", {"start": v(-56.15, 48.18) * mm, "mid": v(-58.99, 44.68) * mm, "end": v(-60, 40.3) * mm});
            skArc(sketch, "E79.17", {"start": v(60, 40.3) * mm, "mid": v(58.99, 44.68) * mm, "end": v(56.15, 48.18) * mm});
            skArc(sketch, "E79.18", {"start": v(56.15, -48.18) * mm, "mid": v(58.99, -44.68) * mm, "end": v(60, -40.3) * mm});
            skArc(sketch, "E79.19", {"start": v(-60, -40.3) * mm, "mid": v(-58.99, -44.68) * mm, "end": v(-56.15, -48.18) * mm});
            skLineSegment(sketch, "E80", {"start": v(33, 90) * mm, "end": v(15, 108) * mm});
            skArc(sketch, "E81", {"start": v(15, 120) * mm, "mid": v(0, 135) * mm, "end": v(-15, 120) * mm});
            skCircle(sketch, "E82", {"center": v(0, 120) * mm, "radius": 6 * mm});
            skLineSegment(sketch, "E83", {"start": v(15, 120) * mm, "end": v(15, 108) * mm});
            skLineSegment(sketch, "E84", {"start": v(-15, 120) * mm, "end": v(-15, 108) * mm});
            skLineSegment(sketch, "E85", {"start": v(-15, 108) * mm, "end": v(-33, 90) * mm});
            skLineSegment(sketch, "E86", {"start": v(-80, 0) * mm, "end": v(80, 0) * mm});
            skLineSegment(sketch, "E87.MirrorCS", {"start": v(15, -120) * mm, "end": v(15, -108) * mm});
            skLineSegment(sketch, "E88.MirrorCS", {"start": v(33, -90) * mm, "end": v(15, -108) * mm});
            skLineSegment(sketch, "E89.MirrorCS", {"start": v(-15, -108) * mm, "end": v(-33, -90) * mm});
            skLineSegment(sketch, "E90.MirrorCS", {"start": v(-15, -120) * mm, "end": v(-15, -108) * mm});
            skCircle(sketch, "E91.MirrorC", {"center": v(0, -120) * mm, "radius": 6 * mm});
            skArc(sketch, "E92.MirrorCS", {"start": v(15, -120) * mm, "mid": v(0, -135) * mm, "end": v(-15, -120) * mm});
            skLineSegment(sketch, "E93", {"start": v(0, 90) * mm, "end": v(0, 120) * mm, "construction": true});
            skSolve(sketch);
        }
        {
            var Q0;
            {var subQ0=sQuery(id+"F16.wireOp",EDGE,"E80");Q0=makeQuery(id+"F16.imprint","IMPRINT",FACE,{"disambiguationData":[TD([[makeQuery(id+"F16.imprint","IMPRINT",EDGE,{"derivedFrom":subQ0}),1.0]])]});}
            var Q1;
            {var subQ9=sQuery(id+"F16.wireOp",EDGE,"E79.1");Q1=makeQuery(id+"F16.imprint","IMPRINT",FACE,{"disambiguationData":[TD([[makeQuery(id+"F16.imprint","IMPRINT",EDGE,{"derivedFrom":subQ9}),1.0]])]});}
            var Q2;
            {var subQ8=sQuery(id+"F16.wireOp",EDGE,"E79.5");Q2=makeQuery(id+"F16.imprint","IMPRINT",FACE,{"disambiguationData":[TD([[makeQuery(id+"F16.imprint","IMPRINT",EDGE,{"derivedFrom":subQ8}),1.0]])]});}
            var Q3;
            Q3=makeQuery(id+"F16.imprint","IMPRINT",FACE,{"disambiguationData":[TD([[makeQuery(id+"F16.imprint","IMPRINT",EDGE,{"derivedFrom":sQuery(id+"F16.wireOp",EDGE,"E87.MirrorCS")}),1.0]])]});
            var Q4;
            Q4=makeQuery(id+"F2.opExtrude","CAP_FACE",FACE,{"disambiguationData":[OSD([sQuery(id+"F0.wireOp",EDGE,"E12"),sQuery(id+"F0.wireOp",EDGE,"E13"),sQuery(id+"F0.wireOp",EDGE,"E14"),sQuery(id+"F0.wireOp",EDGE,"E15"),sQuery(id+"F0.wireOp",EDGE,"E17.filletArc"),sQuery(id+"F0.wireOp",EDGE,"E18.filletArc"),sQuery(id+"F0.wireOp",EDGE,"E19.filletArc"),sQuery(id+"F0.wireOp",EDGE,"E20.filletArc"),sQuery(id+"F0.wireOp",EDGE,"E25.0"),sQuery(id+"F0.wireOp",EDGE,"E25.1"),sQuery(id+"F0.wireOp",EDGE,"E25.2"),sQuery(id+"F0.wireOp",EDGE,"E25.3"),sQuery(id+"F0.wireOp",EDGE,"E25.4"),sQuery(id+"F0.wireOp",EDGE,"E25.5"),sQuery(id+"F0.wireOp",EDGE,"E25.6"),sQuery(id+"F0.wireOp",EDGE,"E25.7")])],"isStart":false});
            extrude(context, id + "F17", {"entities" : qUnion([Q0, Q1, Q2, Q3]), "endBound" : BoundingType.UP_TO_SURFACE, "depth" : 25 * mm, "endBoundEntityFace" : qUnion([Q4]), "offsetDistance" : 25 * mm});
        }
    });
